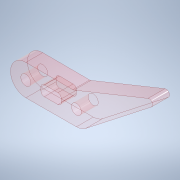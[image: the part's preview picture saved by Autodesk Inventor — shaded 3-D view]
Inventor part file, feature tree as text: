
AUTODESK INVENTOR PART (.ipt)
format: ipt  version: 2020.2 (Build 242310000, 310)  size: 160,256 bytes
history: native  units: mm
features: other x2, extrude x2, fillet x2, sketch x2
ambient origin geometry x8: Origin, YZ Plane, XZ Plane, XY Plane, X Axis, Y Axis, Z Axis, Center Point
bodies: Body1 (feature_tree)
feature tree (8):
  other  "ソリッド1"
  extrude  "押し出し1"  Depth=2.0mm
  fillet  "フィレット1"  Radius=25.0mm
  extrude  "押し出し2"  TaperAngle=150.0deg  [1 undecoded]
  fillet  "フィレット2"  Radius=5.0mm
  sketch  "スケッチ1"
  sketch  "スケッチ2"
  other  "断面エッジを投影1"
note: 1 required parameter value undecoded (feature->parameter linkage not recoverable at this tier; creation-order binding heuristic only, values carry confidence <= 0.55)
